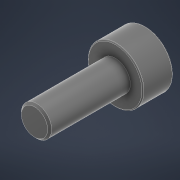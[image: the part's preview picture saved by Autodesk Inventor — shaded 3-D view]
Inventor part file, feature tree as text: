
AUTODESK INVENTOR PART (.ipt)
format: ipt  version: 2022 (Build 260153000, 153)  size: 141,312 bytes
history: native  units: in
note: dims shown in document units (in); Inventor stores cm internally (conversion verified against a paired STEP export)
features: sketch x3, extrude x2, plane x1, fillet x1, chamfer x1
ambient origin geometry x8: Origin, YZ Plane, XZ Plane, XY Plane, X Axis, Y Axis, Z Axis, Center Point
bodies: Body1 (feature_tree)
feature tree (8):
  plane  "Work Plane1"
  fillet  "Fillet1"  [1 undecoded]
  extrude  "Extrusion2"  Depth=0.0039in
  extrude  "Extrusion1"  Depth=0.315in TaperAngle=0.0deg
  chamfer  "Chamfer1"  Distance=0.0079in
  sketch  "Sketch1"  dims[d1=0.1181in d2=0.0in d3=0.0039in]
  sketch  "Sketch2"  dims[d4=0.1181in d5=0.0in d6=0.315in d7=0.0in d8=0.0079in d9=0.0079in d10=17.7165in]
  sketch  "Sketch3"
note: 1 required parameter value undecoded (feature->parameter linkage not recoverable at this tier; creation-order binding heuristic only, values carry confidence <= 0.55)
